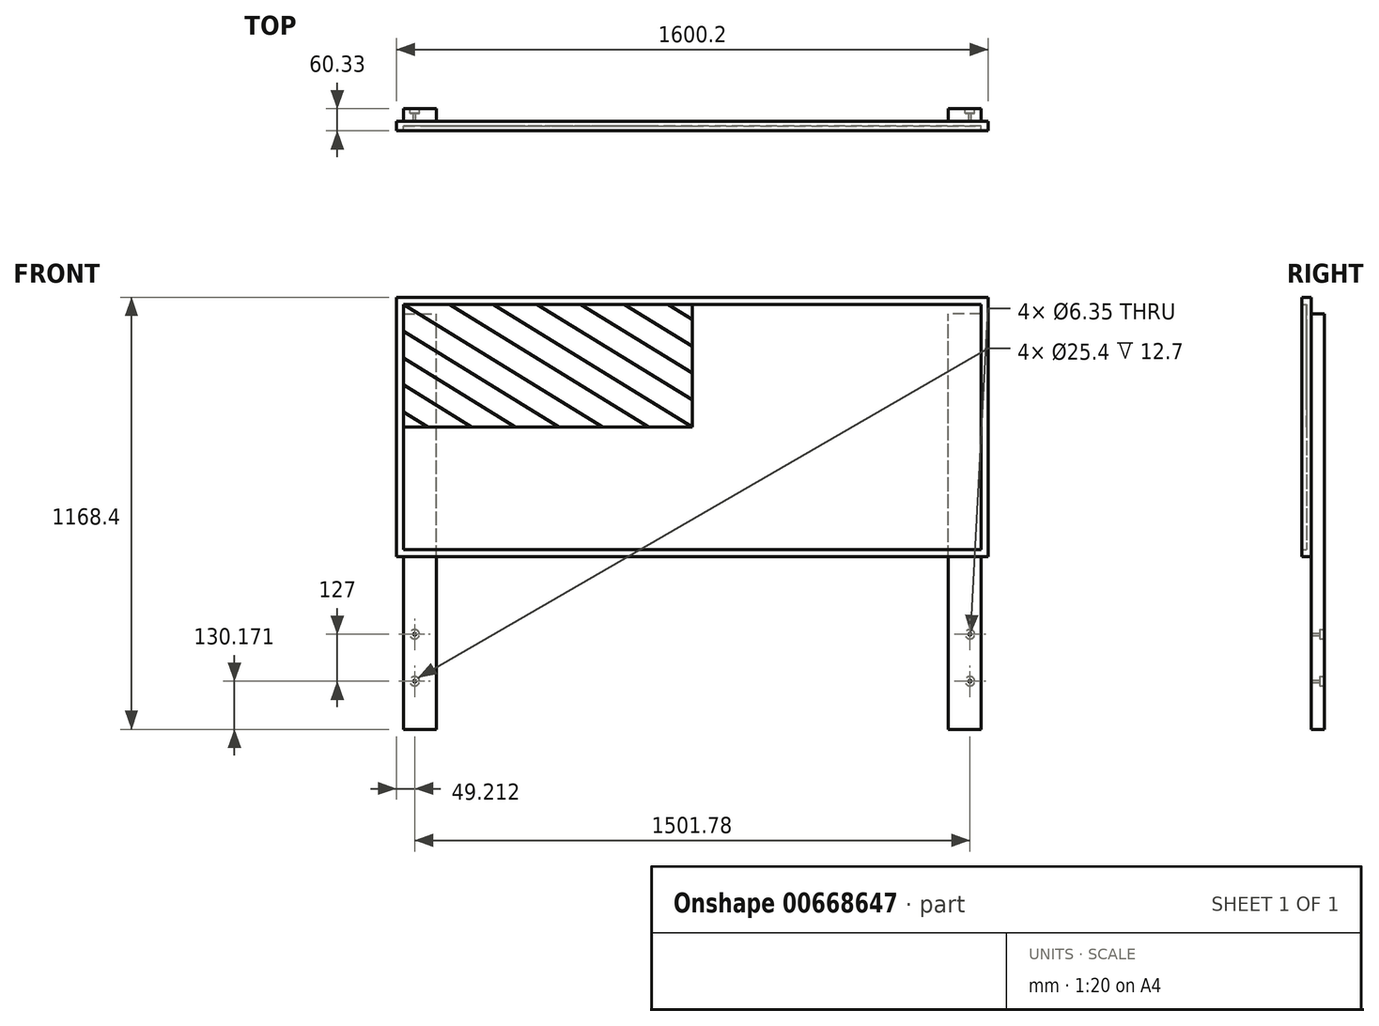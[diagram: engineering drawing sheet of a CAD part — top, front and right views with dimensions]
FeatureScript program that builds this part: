
annotation { "Feature Type Name" : "Feature", "Feature Type Description" : "" }
export const myFeature = defineFeature(function(context is Context, id is Id, definition is map)
    precondition{}
    {
        {
            var Q0;
            Q0=qCreatedBy(makeId("Front.planeOp"),FACE);
            var sketch = newSketch(context, id + "F0", { "sketchPlane" : qUnion([Q0])});
            skLineSegment(sketch, "E0.left", {"start": v(781.05, 331.4) * mm, "end": v(781.05, -331.4) * mm});
            skLineSegment(sketch, "E0.right", {"start": v(-781.05, 331.4) * mm, "end": v(-781.05, -331.4) * mm});
            skPoint(sketch, "E0.middle", {"position": v(0, 0) * mm});
            skLineSegment(sketch, "E1.trimOffspring", {"start": v(781.05, -331.4) * mm, "end": v(-781.05, -331.4) * mm});
            skLineSegment(sketch, "E2", {"start": v(-781.05, 331.4) * mm, "end": v(781.05, 331.4) * mm});
            skLineSegment(sketch, "E3", {"start": v(0, 0) * mm, "end": v(-781.05, 0) * mm, "construction": true});
            skLineSegment(sketch, "E4", {"start": v(0, 0) * mm, "end": v(0, 331.4) * mm, "construction": true});
            skLineSegment(sketch, "E5", {"start": v(-781.05, 331.4) * mm, "end": v(-242.37, 0) * mm, "construction": true});
            skLineSegment(sketch, "E6", {"start": v(0, 0) * mm, "end": v(-538.68, 331.4) * mm, "construction": true});
            skLineSegment(sketch, "E7.0", {"start": v(-121.19, 0) * mm, "end": v(-659.86, 331.4) * mm, "construction": true});
            skLineSegment(sketch, "E8", {"start": v(-781.05, 256.84) * mm, "end": v(-363.56, 0) * mm, "construction": true});
            skLineSegment(sketch, "E9", {"start": v(-781.05, 182.29) * mm, "end": v(-484.75, 0) * mm, "construction": true});
            skLineSegment(sketch, "E10", {"start": v(-781.05, 107.73) * mm, "end": v(-605.93, 0) * mm, "construction": true});
            skLineSegment(sketch, "E11", {"start": v(-417.5, 331.4) * mm, "end": v(0, 74.55) * mm, "construction": true});
            skLineSegment(sketch, "E12", {"start": v(-296.3, 331.4) * mm, "end": v(0, 149.1) * mm, "construction": true});
            skLineSegment(sketch, "E13", {"start": v(-175.12, 331.4) * mm, "end": v(0, 223.66) * mm, "construction": true});
            skLineSegment(sketch, "E14", {"start": v(-53.93, 331.4) * mm, "end": v(0, 298.22) * mm, "construction": true});
            skLineSegment(sketch, "E15", {"start": v(-727.12, 0) * mm, "end": v(-781.05, 33.18) * mm, "construction": true});
            skLineSegment(sketch, "E16", {"start": v(-781.05, 256.84) * mm, "end": v(-781.05, 299.1) * mm, "construction": true});
            skLineSegment(sketch, "E17", {"start": v(-242.37, 0) * mm, "end": v(-319.72, -125.73) * mm, "construction": true});
            skLineSegment(sketch, "E18", {"start": v(-363.56, 0) * mm, "end": v(-440.9, -125.73) * mm, "construction": true});
            skLineSegment(sketch, "E19", {"start": v(-484.75, 0) * mm, "end": v(-562.1, -125.73) * mm, "construction": true});
            skLineSegment(sketch, "E20", {"start": v(-605.93, 0) * mm, "end": v(-683.28, -125.73) * mm, "construction": true});
            skLineSegment(sketch, "E21", {"start": v(-727.12, 0) * mm, "end": v(-804.47, -125.73) * mm, "construction": true});
            skLineSegment(sketch, "E22", {"start": v(-121.19, 0) * mm, "end": v(-198.53, -125.73) * mm, "construction": true});
            skLineSegment(sketch, "E23", {"start": v(0, 0) * mm, "end": v(-77.35, -125.73) * mm, "construction": true});
            skSolve(sketch);
        }
        {
            var Q0;
            Q0 = qSketchRegion(id + "F0", true);
            extrude(context, id + "F1", {"entities" : qUnion([Q0]), "depth" : 12.7 * mm, "offsetDistance" : 25.4 * mm});
        }
        {
            var Q0;
            Q0=qCreatedBy(makeId("Front.planeOp"),FACE);
            var sketch = newSketch(context, id + "F2", { "sketchPlane" : qUnion([Q0])});
            skLineSegment(sketch, "E24.bottom", {"start": v(-781.05, -331.4) * mm, "end": v(781.05, -331.4) * mm});
            skLineSegment(sketch, "E24.top", {"start": v(-781.05, 331.4) * mm, "end": v(781.05, 331.4) * mm});
            skLineSegment(sketch, "E24.left", {"start": v(-781.05, -331.4) * mm, "end": v(-781.05, 331.4) * mm});
            skLineSegment(sketch, "E24.right", {"start": v(781.05, -331.4) * mm, "end": v(781.05, 331.4) * mm});
            skLineSegment(sketch, "E25.bottom", {"start": v(-800.1, -350.45) * mm, "end": v(800.1, -350.45) * mm});
            skLineSegment(sketch, "E25.top", {"start": v(-800.1, 350.45) * mm, "end": v(800.1, 350.45) * mm});
            skLineSegment(sketch, "E25.left", {"start": v(-800.1, -350.45) * mm, "end": v(-800.1, 350.45) * mm});
            skLineSegment(sketch, "E25.right", {"start": v(800.1, -350.45) * mm, "end": v(800.1, 350.45) * mm});
            skSolve(sketch);
        }
        {
            var Q0;
            Q0 = qSketchRegion(id + "F2", true);
            extrude(context, id + "F3", {"entities" : qUnion([Q0]), "operationType" : NewBodyOperationType.ADD, "depth" : 25.4 * mm, "offsetDistance" : 25.4 * mm});
        }
        {
            var Q0;
            Q0=makeQuery(id+"F1.opExtrude","CAP_FACE",FACE,{"disambiguationData":[OSD([sQuery(id+"F0.wireOp",EDGE,"E0.left"),sQuery(id+"F0.wireOp",EDGE,"E0.right"),sQuery(id+"F0.wireOp",EDGE,"E1.trimOffspring"),sQuery(id+"F0.wireOp",EDGE,"E2")])],"isStart":false});
            var sketch = newSketch(context, id + "F4", { "sketchPlane" : qUnion([Q0])});
            skLineSegment(sketch, "E26", {"start": v(0, 0) * mm, "end": v(-538.68, 331.4) * mm});
            skLineSegment(sketch, "E27", {"start": v(-781.05, 331.4) * mm, "end": v(-242.37, 0) * mm});
            skLineSegment(sketch, "E28", {"start": v(-538.68, 331.4) * mm, "end": v(-656.83, 331.4) * mm});
            skLineSegment(sketch, "E29", {"start": v(-656.83, 331.4) * mm, "end": v(-118.16, 0) * mm});
            skLineSegment(sketch, "E30", {"start": v(-118.16, 0) * mm, "end": v(0, 0) * mm});
            skLineSegment(sketch, "E31", {"start": v(-242.37, 0) * mm, "end": v(-360.53, 0) * mm});
            skLineSegment(sketch, "E32", {"start": v(-360.53, 0) * mm, "end": v(-781.05, 258.7) * mm});
            skLineSegment(sketch, "E33", {"start": v(-781.05, 258.7) * mm, "end": v(-781.05, 331.4) * mm});
            skLineSegment(sketch, "E34", {"start": v(-478.69, 0) * mm, "end": v(-781.05, 186.02) * mm});
            skLineSegment(sketch, "E35", {"start": v(-781.05, 186.02) * mm, "end": v(-781.05, 113.32) * mm});
            skLineSegment(sketch, "E36", {"start": v(-781.05, 113.32) * mm, "end": v(-596.84, 0) * mm});
            skLineSegment(sketch, "E37", {"start": v(-596.84, 0) * mm, "end": v(-478.69, 0) * mm});
            skLineSegment(sketch, "E38", {"start": v(-715, 0) * mm, "end": v(-781.05, 40.63) * mm});
            skLineSegment(sketch, "E39", {"start": v(0, 72.7) * mm, "end": v(-420.52, 331.4) * mm});
            skLineSegment(sketch, "E40", {"start": v(-420.52, 331.4) * mm, "end": v(-302.36, 331.4) * mm});
            skLineSegment(sketch, "E41", {"start": v(-302.36, 331.4) * mm, "end": v(0, 145.38) * mm});
            skLineSegment(sketch, "E42", {"start": v(0, 145.38) * mm, "end": v(0, 72.7) * mm});
            skLineSegment(sketch, "E43", {"start": v(-715, 0) * mm, "end": v(-781.05, 0) * mm});
            skLineSegment(sketch, "E44", {"start": v(-781.05, 0) * mm, "end": v(-781.05, 40.63) * mm});
            skLineSegment(sketch, "E45", {"start": v(0, 218.07) * mm, "end": v(-184.2, 331.4) * mm});
            skLineSegment(sketch, "E46", {"start": v(-66.05, 331.4) * mm, "end": v(0, 290.76) * mm});
            skLineSegment(sketch, "E47", {"start": v(0, 290.76) * mm, "end": v(0, 218.07) * mm});
            skLineSegment(sketch, "E48", {"start": v(-184.2, 331.4) * mm, "end": v(-66.05, 331.4) * mm});
            skSolve(sketch);
        }
        {
            var Q0;
            Q0 = qSketchRegion(id + "F4", true);
            extrude(context, id + "F5", {"entities" : qUnion([Q0]), "operationType" : NewBodyOperationType.ADD, "depth" : 0.03 * mm, "offsetDistance" : 25.4 * mm});
        }
        {
            var Q0;
            Q0=makeQuery(id+"F1.opExtrude","CAP_FACE",FACE,{"disambiguationData":[OSD([sQuery(id+"F0.wireOp",EDGE,"E0.left"),sQuery(id+"F0.wireOp",EDGE,"E0.right"),sQuery(id+"F0.wireOp",EDGE,"E1.trimOffspring"),sQuery(id+"F0.wireOp",EDGE,"E2")])],"isStart":false});
            var sketch = newSketch(context, id + "F6", { "sketchPlane" : qUnion([Q0])});
            skLineSegment(sketch, "E49", {"start": v(-781.05, 113.32) * mm, "end": v(-781.05, 40.63) * mm});
            skLineSegment(sketch, "E50", {"start": v(-781.05, 40.63) * mm, "end": v(-715, 0) * mm});
            skLineSegment(sketch, "E51", {"start": v(-715, 0) * mm, "end": v(-596.84, 0) * mm});
            skLineSegment(sketch, "E52", {"start": v(-596.84, 0) * mm, "end": v(-781.05, 113.32) * mm});
            skLineSegment(sketch, "E53", {"start": v(-781.05, 186.02) * mm, "end": v(-781.05, 258.7) * mm});
            skLineSegment(sketch, "E54", {"start": v(-781.05, 258.7) * mm, "end": v(-360.53, 0) * mm});
            skLineSegment(sketch, "E55", {"start": v(-360.53, 0) * mm, "end": v(-478.69, 0) * mm});
            skLineSegment(sketch, "E56", {"start": v(-478.69, 0) * mm, "end": v(-781.05, 186.02) * mm});
            skLineSegment(sketch, "E57", {"start": v(-781.05, 331.4) * mm, "end": v(-656.83, 331.4) * mm});
            skLineSegment(sketch, "E58", {"start": v(-656.83, 331.4) * mm, "end": v(-118.16, 0) * mm});
            skLineSegment(sketch, "E59", {"start": v(-118.16, 0) * mm, "end": v(-242.37, 0) * mm});
            skLineSegment(sketch, "E60", {"start": v(-242.37, 0) * mm, "end": v(-781.05, 331.4) * mm});
            skLineSegment(sketch, "E61", {"start": v(-538.68, 331.4) * mm, "end": v(-420.52, 331.4) * mm});
            skLineSegment(sketch, "E62", {"start": v(-420.52, 331.4) * mm, "end": v(0, 72.7) * mm});
            skLineSegment(sketch, "E63", {"start": v(0, 72.7) * mm, "end": v(0, 0) * mm});
            skLineSegment(sketch, "E64", {"start": v(0, 0) * mm, "end": v(-538.68, 331.4) * mm});
            skLineSegment(sketch, "E65", {"start": v(-302.36, 331.4) * mm, "end": v(-184.2, 331.4) * mm});
            skLineSegment(sketch, "E66", {"start": v(-184.2, 331.4) * mm, "end": v(0, 218.07) * mm});
            skLineSegment(sketch, "E67", {"start": v(0, 218.07) * mm, "end": v(0, 145.38) * mm});
            skLineSegment(sketch, "E68", {"start": v(0, 145.38) * mm, "end": v(-302.36, 331.4) * mm});
            skLineSegment(sketch, "E69", {"start": v(-66.05, 331.4) * mm, "end": v(0, 331.4) * mm});
            skLineSegment(sketch, "E70", {"start": v(0, 331.4) * mm, "end": v(0, 290.76) * mm});
            skLineSegment(sketch, "E71", {"start": v(0, 290.76) * mm, "end": v(-66.05, 331.4) * mm});
            skSolve(sketch);
        }
        {
            var Q0;
            Q0 = qSketchRegion(id + "F6", true);
            extrude(context, id + "F7", {"entities" : qUnion([Q0]), "operationType" : NewBodyOperationType.ADD, "depth" : 0.05 * mm, "offsetDistance" : 25.4 * mm});
        }
        {
            var Q0;
            Q0=qCreatedBy(makeId("Front.planeOp"),FACE);
            var sketch = newSketch(context, id + "F8", { "sketchPlane" : qUnion([Q0])});
            skLineSegment(sketch, "E72.bottom", {"start": v(781.05, -817.95) * mm, "end": v(692.15, -817.95) * mm});
            skLineSegment(sketch, "E72.top", {"start": v(781.05, 306) * mm, "end": v(692.15, 306) * mm});
            skLineSegment(sketch, "E72.left", {"start": v(781.05, -817.95) * mm, "end": v(781.05, 306) * mm});
            skLineSegment(sketch, "E72.right", {"start": v(692.15, -817.95) * mm, "end": v(692.15, 306) * mm});
            skLineSegment(sketch, "E73.MirrorCS", {"start": v(-692.15, -817.95) * mm, "end": v(-692.15, 306) * mm});
            skLineSegment(sketch, "E74.MirrorCS", {"start": v(-781.05, 306) * mm, "end": v(-692.15, 306) * mm});
            skLineSegment(sketch, "E75.MirrorCS", {"start": v(-781.05, -817.95) * mm, "end": v(-781.05, 306) * mm});
            skLineSegment(sketch, "E76.MirrorCS", {"start": v(-781.05, -817.95) * mm, "end": v(-692.15, -817.95) * mm});
            skSolve(sketch);
        }
        {
            var Q0;
            Q0 = qSketchRegion(id + "F8", true);
            extrude(context, id + "F9", {"entities" : qUnion([Q0]), "operationType" : NewBodyOperationType.ADD, "oppositeDirection" : true, "depth" : 34.92 * mm, "offsetDistance" : 25.4 * mm});
        }
        {
            var Q0;
            Q0=makeQuery(id+"F9.opExtrude","CAP_FACE",FACE,{"disambiguationData":[OSD([sQuery(id+"F8.wireOp",EDGE,"E72.bottom"),sQuery(id+"F8.wireOp",EDGE,"E72.top"),sQuery(id+"F8.wireOp",EDGE,"E72.left"),sQuery(id+"F8.wireOp",EDGE,"E72.right")])],"isStart":false});
            var sketch = newSketch(context, id + "F10", { "sketchPlane" : qUnion([Q0])});
            skCircle(sketch, "E77", {"center": v(-750.89, -687.78) * mm, "radius": 3.18 * mm});
            skLineSegment(sketch, "E78", {"start": v(0, 0) * mm, "end": v(-899.03, 0) * mm, "construction": true});
            skLineSegment(sketch, "E79", {"start": v(0, 0) * mm, "end": v(0, -673.54) * mm, "construction": true});
            skLineSegment(sketch, "E80.bottom", {"start": v(-769.94, -700.48) * mm, "end": v(-731.84, -700.48) * mm, "construction": true});
            skLineSegment(sketch, "E80.top", {"start": v(-769.94, -548.08) * mm, "end": v(-731.84, -548.08) * mm, "construction": true});
            skLineSegment(sketch, "E80.left", {"start": v(-769.94, -700.48) * mm, "end": v(-769.94, -548.08) * mm, "construction": true});
            skLineSegment(sketch, "E80.right", {"start": v(-731.84, -700.48) * mm, "end": v(-731.84, -548.08) * mm, "construction": true});
            skLineSegment(sketch, "E81.bottom", {"start": v(-744.54, -684.6) * mm, "end": v(-757.24, -684.6) * mm, "construction": true});
            skLineSegment(sketch, "E81.top", {"start": v(-744.54, -690.95) * mm, "end": v(-757.24, -690.95) * mm, "construction": true});
            skArc(sketch, "E82", {"start": v(-757.24, -690.95) * mm, "mid": v(-760.41, -687.78) * mm, "end": v(-757.24, -684.6) * mm, "construction": true});
            skArc(sketch, "E83", {"start": v(-744.54, -684.6) * mm, "mid": v(-741.36, -687.78) * mm, "end": v(-744.54, -690.95) * mm, "construction": true});
            skArc(sketch, "E84.1.0.0", {"start": v(-757.24, -678.25) * mm, "mid": v(-760.41, -675.08) * mm, "end": v(-757.24, -671.9) * mm, "construction": true});
            skLineSegment(sketch, "E84.1.0.1", {"start": v(-744.54, -678.25) * mm, "end": v(-757.24, -678.25) * mm, "construction": true});
            skArc(sketch, "E84.1.0.2", {"start": v(-744.54, -671.9) * mm, "mid": v(-741.36, -675.08) * mm, "end": v(-744.54, -678.25) * mm, "construction": true});
            skLineSegment(sketch, "E84.1.0.3", {"start": v(-744.54, -671.9) * mm, "end": v(-757.24, -671.9) * mm, "construction": true});
            skArc(sketch, "E84.2.0.0", {"start": v(-757.24, -665.55) * mm, "mid": v(-760.41, -662.38) * mm, "end": v(-757.24, -659.2) * mm, "construction": true});
            skLineSegment(sketch, "E84.2.0.1", {"start": v(-744.54, -665.55) * mm, "end": v(-757.24, -665.55) * mm, "construction": true});
            skArc(sketch, "E84.2.0.2", {"start": v(-744.54, -659.2) * mm, "mid": v(-741.36, -662.38) * mm, "end": v(-744.54, -665.55) * mm, "construction": true});
            skLineSegment(sketch, "E84.2.0.3", {"start": v(-744.54, -659.2) * mm, "end": v(-757.24, -659.2) * mm, "construction": true});
            skLineSegment(sketch, "E84.direction1", {"start": v(-757.24, -690.95) * mm, "end": v(-757.24, -678.25) * mm, "construction": true});
            skLineSegment(sketch, "E85", {"start": v(-744.54, -687.78) * mm, "end": v(-744.54, -662.38) * mm, "construction": true});
            skLineSegment(sketch, "E86", {"start": v(-731.84, -624.28) * mm, "end": v(-769.94, -624.28) * mm, "construction": true});
            skArc(sketch, "E87.MirrorCS", {"start": v(-744.54, -576.65) * mm, "mid": v(-741.36, -573.48) * mm, "end": v(-744.54, -570.3) * mm, "construction": true});
            skArc(sketch, "E88.MirrorCS", {"start": v(-744.54, -563.95) * mm, "mid": v(-741.36, -560.78) * mm, "end": v(-744.54, -557.6) * mm, "construction": true});
            skArc(sketch, "E89.MirrorCS", {"start": v(-744.54, -589.35) * mm, "mid": v(-741.36, -586.18) * mm, "end": v(-744.54, -583) * mm, "construction": true});
            skLineSegment(sketch, "E90.MirrorCS", {"start": v(-744.54, -560.78) * mm, "end": v(-744.54, -586.18) * mm, "construction": true});
            skArc(sketch, "E91.MirrorCS", {"start": v(-757.24, -557.6) * mm, "mid": v(-760.41, -560.78) * mm, "end": v(-757.24, -563.95) * mm, "construction": true});
            skPoint(sketch, "E92.MirrorP", {"position": v(-750.89, -560.78) * mm});
            skArc(sketch, "E93.MirrorCS", {"start": v(-757.24, -570.3) * mm, "mid": v(-760.41, -573.48) * mm, "end": v(-757.24, -576.65) * mm, "construction": true});
            skLineSegment(sketch, "E94.MirrorCS", {"start": v(-744.54, -589.35) * mm, "end": v(-757.24, -589.35) * mm, "construction": true});
            skArc(sketch, "E95.MirrorCS", {"start": v(-757.24, -583) * mm, "mid": v(-760.41, -586.18) * mm, "end": v(-757.24, -589.35) * mm, "construction": true});
            skLineSegment(sketch, "E96.MirrorCS", {"start": v(-744.54, -557.6) * mm, "end": v(-757.24, -557.6) * mm, "construction": true});
            skLineSegment(sketch, "E97.MirrorCS", {"start": v(-744.54, -570.3) * mm, "end": v(-757.24, -570.3) * mm, "construction": true});
            skLineSegment(sketch, "E98.MirrorCS", {"start": v(-744.54, -576.65) * mm, "end": v(-757.24, -576.65) * mm, "construction": true});
            skLineSegment(sketch, "E99.MirrorCS", {"start": v(-757.24, -557.6) * mm, "end": v(-757.24, -570.3) * mm, "construction": true});
            skLineSegment(sketch, "E100.MirrorCS", {"start": v(-744.54, -583) * mm, "end": v(-757.24, -583) * mm, "construction": true});
            skCircle(sketch, "E101.MirrorC", {"center": v(-750.89, -560.78) * mm, "radius": 3.18 * mm});
            skCircle(sketch, "E102.MirrorC", {"center": v(750.89, -560.78) * mm, "radius": 3.18 * mm});
            skCircle(sketch, "E103.MirrorC", {"center": v(750.89, -687.78) * mm, "radius": 3.18 * mm});
            skSolve(sketch);
        }
        {
            var Q0;
            Q0 = qSketchRegion(id + "F10", true);
            extrude(context, id + "F11", {"entities" : qUnion([Q0]), "operationType" : NewBodyOperationType.REMOVE, "endBound" : BoundingType.THROUGH_ALL, "oppositeDirection" : true, "depth" : 25.4 * mm, "offsetDistance" : 25.4 * mm});
        }
        {
            var Q0;
            Q0=makeQuery(id+"F9.opExtrude","CAP_FACE",FACE,{"disambiguationData":[OSD([sQuery(id+"F8.wireOp",EDGE,"E72.bottom"),sQuery(id+"F8.wireOp",EDGE,"E72.top"),sQuery(id+"F8.wireOp",EDGE,"E72.left"),sQuery(id+"F8.wireOp",EDGE,"E72.right")])],"isStart":false});
            var sketch = newSketch(context, id + "F12", { "sketchPlane" : qUnion([Q0])});
            skCircle(sketch, "E104", {"center": v(-750.89, -687.78) * mm, "radius": 12.7 * mm});
            skCircle(sketch, "E105", {"center": v(-750.89, -560.78) * mm, "radius": 12.7 * mm});
            skCircle(sketch, "E106.MirrorC", {"center": v(750.89, -687.78) * mm, "radius": 12.7 * mm});
            skCircle(sketch, "E107.MirrorC", {"center": v(750.89, -560.78) * mm, "radius": 12.7 * mm});
            skSolve(sketch);
        }
        {
            var Q0;
            Q0 = qSketchRegion(id + "F12", true);
            extrude(context, id + "F13", {"entities" : qUnion([Q0]), "operationType" : NewBodyOperationType.REMOVE, "oppositeDirection" : true, "depth" : 12.7 * mm, "offsetDistance" : 25.4 * mm});
        }
    });
